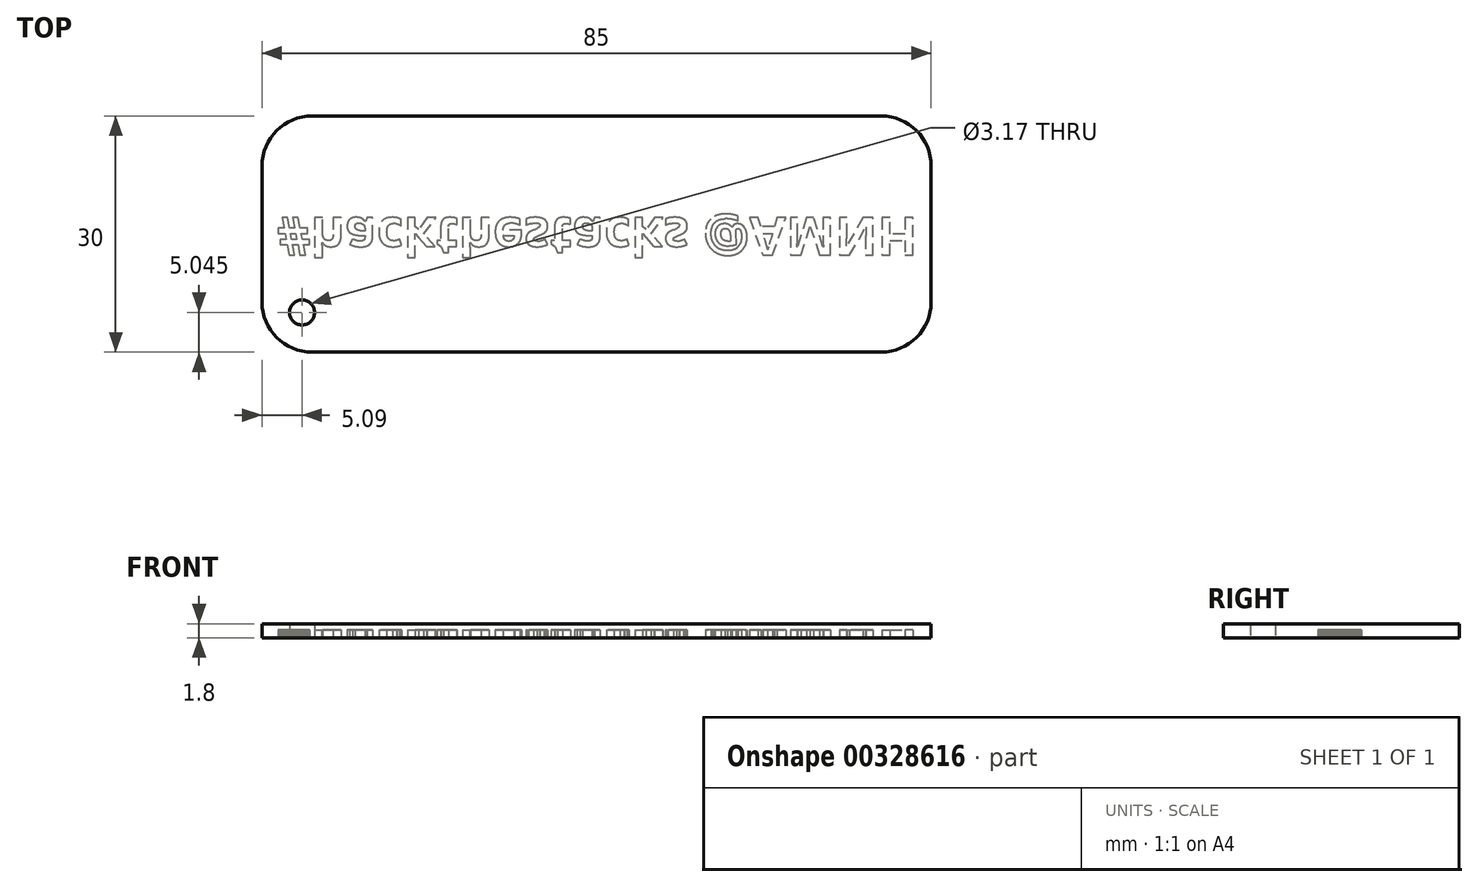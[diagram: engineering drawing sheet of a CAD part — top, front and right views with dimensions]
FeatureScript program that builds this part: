
annotation { "Feature Type Name" : "Feature", "Feature Type Description" : "" }
export const myFeature = defineFeature(function(context is Context, id is Id, definition is map)
    precondition{}
    {
        {
            var Q0;
            Q0=qCreatedBy(makeId("Top.planeOp"),FACE);
            var sketch = newSketch(context, id + "F0", { "sketchPlane" : qUnion([Q0])});
            skLineSegment(sketch, "E0.bottom", {"start": v(-32.74, 15.94) * mm, "end": v(39.56, 15.94) * mm});
            skLineSegment(sketch, "E0.top", {"start": v(-32.74, -14.06) * mm, "end": v(39.56, -14.06) * mm});
            skLineSegment(sketch, "E0.left", {"start": v(-39.09, 9.6) * mm, "end": v(-39.09, -7.7) * mm});
            skLineSegment(sketch, "E0.right", {"start": v(45.91, 9.6) * mm, "end": v(45.91, -7.7) * mm});
            skPoint(sketch, "E1.visualSharp", {"position": v(45.91, 15.94) * mm});
            skArc(sketch, "E1.filletArc", {"start": v(45.91, 9.6) * mm, "mid": v(44.05, 14.08) * mm, "end": v(39.56, 15.94) * mm});
            skPoint(sketch, "E2.visualSharp", {"position": v(45.91, -14.06) * mm});
            skArc(sketch, "E2.filletArc", {"start": v(39.56, -14.06) * mm, "mid": v(44.05, -12.2) * mm, "end": v(45.91, -7.7) * mm});
            skPoint(sketch, "E3.visualSharp", {"position": v(-39.09, 15.94) * mm});
            skArc(sketch, "E3.filletArc", {"start": v(-32.74, 15.94) * mm, "mid": v(-37.23, 14.08) * mm, "end": v(-39.09, 9.6) * mm});
            skPoint(sketch, "E4.visualSharp", {"position": v(-39.09, -14.06) * mm});
            skArc(sketch, "E4.filletArc", {"start": v(-39.09, -7.7) * mm, "mid": v(-37.23, -12.2) * mm, "end": v(-32.74, -14.06) * mm});
            skSolve(sketch);
        }
        {
            var Q0;
            Q0=makeQuery(id+"F0.imprint","IMPRINT",FACE,{"disambiguationData":[TD([[makeQuery(id+"F0.imprint","IMPRINT",EDGE,{"derivedFrom":sQuery(id+"F0.wireOp",EDGE,"E0.bottom")}),-1.0]])]});
            extrude(context, id + "F1", {"entities" : qUnion([Q0]), "depth" : 1.8 * mm});
        }
        {
            var Q0;
            Q0=makeQuery(id+"F1.opExtrude","CAP_FACE",FACE,{"disambiguationData":[OSD([sQuery(id+"F0.wireOp",EDGE,"E0.bottom"),sQuery(id+"F0.wireOp",EDGE,"E0.top"),sQuery(id+"F0.wireOp",EDGE,"E0.left"),sQuery(id+"F0.wireOp",EDGE,"E0.right"),sQuery(id+"F0.wireOp",EDGE,"E1.filletArc"),sQuery(id+"F0.wireOp",EDGE,"E2.filletArc"),sQuery(id+"F0.wireOp",EDGE,"E3.filletArc"),sQuery(id+"F0.wireOp",EDGE,"E4.filletArc")])],"isStart":true});
            var sketch = newSketch(context, id + "F2", { "sketchPlane" : qUnion([Q0])});
            skCircle(sketch, "E5", {"center": v(-34, 9.02) * mm, "radius": 1.59 * mm});
            skSolve(sketch);
        }
        {
            var Q0;
            Q0 = qSketchRegion(id + "F2", true);
            extrude(context, id + "F3", {"entities" : qUnion([Q0]), "operationType" : NewBodyOperationType.REMOVE, "oppositeDirection" : true, "depth" : 25.4 * mm});
        }
        {
            var Q0;
            Q0=makeQuery(id+"F1.opExtrude","CAP_FACE",FACE,{"disambiguationData":[OSD([sQuery(id+"F0.wireOp",EDGE,"E0.bottom"),sQuery(id+"F0.wireOp",EDGE,"E0.top"),sQuery(id+"F0.wireOp",EDGE,"E0.left"),sQuery(id+"F0.wireOp",EDGE,"E0.right"),sQuery(id+"F0.wireOp",EDGE,"E1.filletArc"),sQuery(id+"F0.wireOp",EDGE,"E2.filletArc"),sQuery(id+"F0.wireOp",EDGE,"E3.filletArc"),sQuery(id+"F0.wireOp",EDGE,"E4.filletArc")])],"isStart":true});
            var sketch = newSketch(context, id + "F4", { "sketchPlane" : qUnion([Q0])});
            skText(sketch, "E6", { "text": "#hackthestacks @AMNH", "fontName": "OpenSans-Bold.ttf"});
            const initialGuessF4  = {"E6": [-0.0372, -0.00301, 1, 0, 0.00478]};
            skSetInitialGuess(sketch, initialGuessF4);
            skSolve(sketch);
        }
        {
            var Q0;
            Q0 = qSketchRegion(id + "F4", true);
            extrude(context, id + "F5", {"entities" : qUnion([Q0]), "operationType" : NewBodyOperationType.REMOVE, "oppositeDirection" : true, "depth" : 1 * mm});
        }
    });
